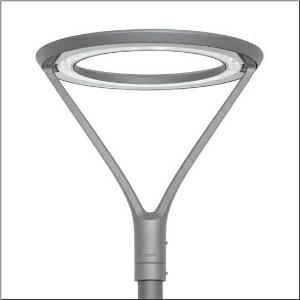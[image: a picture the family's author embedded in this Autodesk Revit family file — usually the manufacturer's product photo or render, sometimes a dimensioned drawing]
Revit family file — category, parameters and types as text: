
# Revit family: dl_20___p1_0a_5xa512836r008_f2c4
name_source: partatom
category: Lighting Fixtures
units: mm (PartAtom-declared; Revit-internal decimal feet)

## family parameters
Cut with Voids When Loaded = No
Host = Face
Light Source = No
Part Type = Normal
Room Calculation Point = No
Round Connector Dimension = Use Diameter
Shared = No

## types (1)
- --- (1 x LED, 3030 lm, 28.6 W, 2700K)
    Apparent Load = 29 VA
    CIE Flux Codes = 31 71 96 100 100
    Color Rendering = 70
    Color Temperature = 2700K
    Default Elevation = 1800 mm
    Description = DL® 20, mast luminaire, primary light control with cycle path optic, highly specular, primary optical cover: cover, of toughened safety glass of clear glass with excellent transmission level, light distribution: P1.0a, light emission: direct distribution, primary light characteristic: asymmetric, installation type: post-top, LED, High Power LED, rated luminous flux: 3.030lm, luminous efficacy: 106lm/W, light colour: 727, colour temperature: 2700K, control gear: Plus, control: flexible luminous flux parameterisation, time-dependent luminous flux control, constant luminous flux control, digital communication interface, power reduction, overheat protection, electronic power reduction, mains connection: 220..240V, 50/60Hz, connection cable pre-assembled, cable length: 5m, start of lifetime: 29W, end of service life: 29W, reduction: 15W, luminaire housing, upper part, of cast aluminium, powder-coated, Siteco® metallic grey (DB 702S), diameter: 690mm, height: 690mm, spigot size: 76mm (post-top), mounting height: 4..6m, luminaire housing, of cast aluminium, powder-coated, Siteco® metallic grey (DB 702S), equipment: standard, protection rating (complete): IP66, insulation class (complete): insulation class II (safety insulation), certification: CE, ENEC, VDE, impact resistance: IK08, permissible operating ambient temperature: -25..+35°C, standard-compliant lighting for roads and squares, packaging unit: 1 piece

Light Distribution: P1.0a
    Height = 690 mm
    Lamp = 1 x LED
    Lamp Light Flux = 3030 lm
    Lamp Power = 28.6 W
    Lamp count = 1
    Length = 690 mm
    Luminous efficacy = 106 lm/W
    Manufacturer = Siteco
    ModVariant = No
    Model = 5XA512836R008
    Number of Poles = 1
    OnlyDefault = Yes
    Power Factor = 1
    Product Name = DL 20 | P1.0a
    Product group = mast luminaire | pylon top
    ProductGroupID = 6100
    Protection Class = Protection class II
    Protection Degree = IP 66
    RLX_Detail_Level = 1
    RLX_Emergency_Light_Flux = 0 lm
    RLX_Emergency_Type = 0
    RLX_Emergency_Type_DB = No
    RlxData = <blob elided: 206881 chars, md5=bde8fccd>
    Socket = socket
    Standby Power = 0 W
    System Light Flux = 3030 lm
    System Power = 29 W
    Type Comments = factory setting: luminous flux: 100 % | dim-lin: 254 | 386 mA
    Type Image = l_1006001.jpg
    URL = http://relux.com
    VarID = @adj_084821
    Voltage = 0 V
    Weight = 0.00 kg
    Width = 0 mm  [stored 0 ft]

note: [stored X ft] marks values corroborated as IEEE doubles in the binary element streams (Revit-internal decimal feet)

## geometry (parser evidence)
native form markers: Blend x4, Sweep x11
no freeform markers — native parametric forms only
